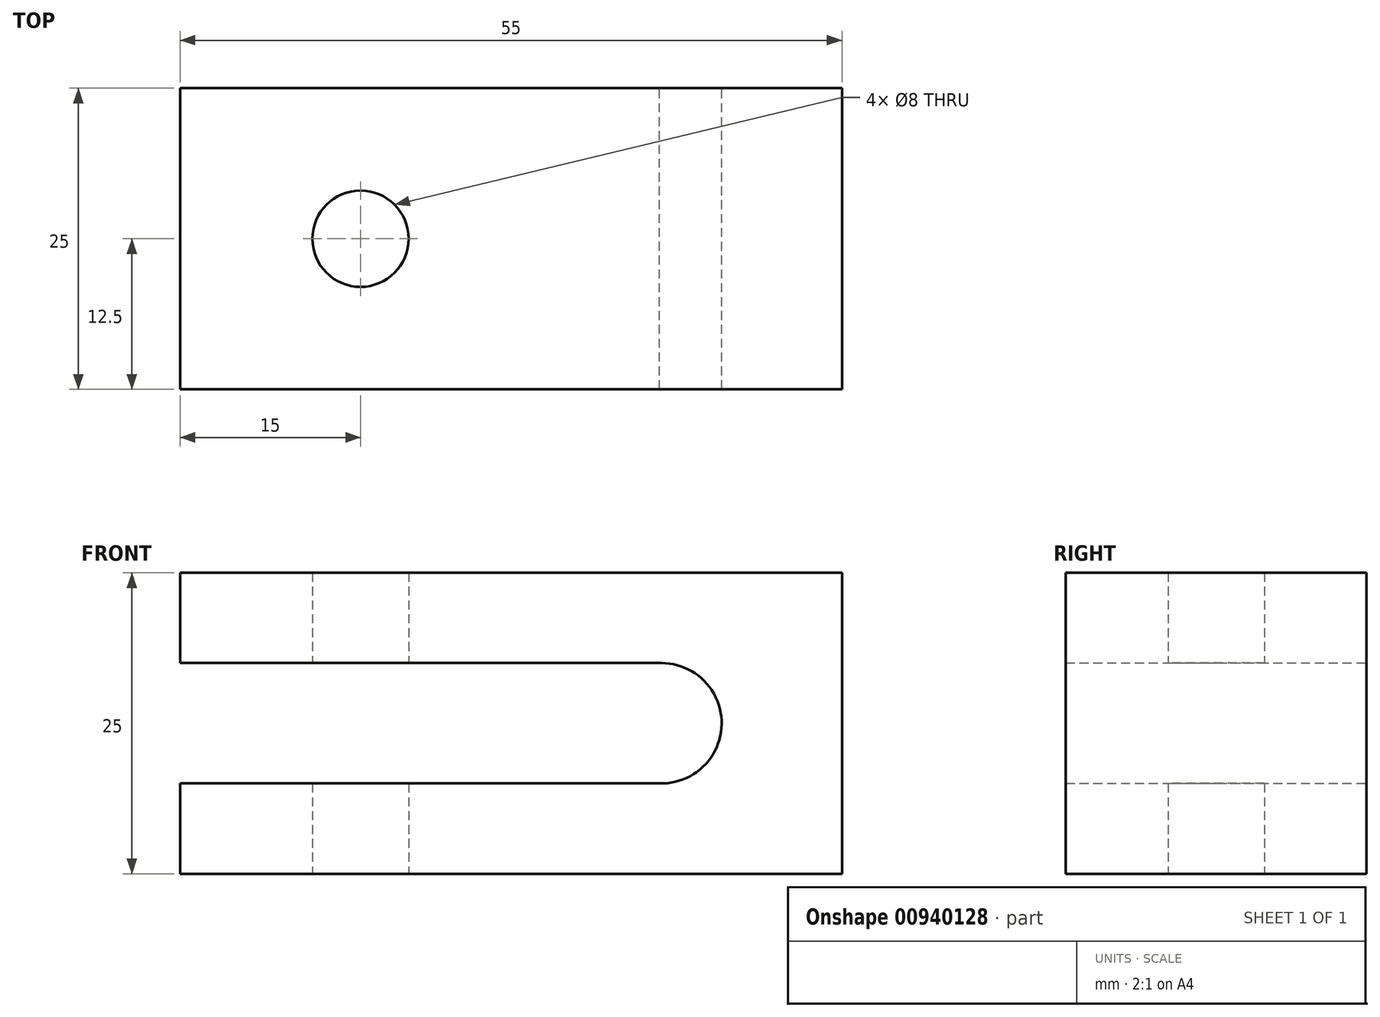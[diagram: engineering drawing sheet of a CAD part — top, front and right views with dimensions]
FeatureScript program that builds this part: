
annotation { "Feature Type Name" : "Feature", "Feature Type Description" : "" }
export const myFeature = defineFeature(function(context is Context, id is Id, definition is map)
    precondition{}
    {
        {
            var Q0;
            Q0=qCreatedBy(makeId("Front.planeOp"),FACE);
            var sketch = newSketch(context, id + "F0", { "sketchPlane" : qUnion([Q0])});
            skLineSegment(sketch, "E0.bottom", {"start": v(-27.5, 12.5) * mm, "end": v(27.5, 12.5) * mm});
            skLineSegment(sketch, "E0.top", {"start": v(-27.5, -12.5) * mm, "end": v(27.5, -12.5) * mm});
            skLineSegment(sketch, "E0.left", {"start": v(-27.5, 12.5) * mm, "end": v(-27.5, 5) * mm});
            skLineSegment(sketch, "E0.right", {"start": v(27.5, 12.5) * mm, "end": v(27.5, -12.5) * mm});
            skPoint(sketch, "E0.middle", {"position": v(0, 0) * mm});
            skArc(sketch, "E1", {"start": v(12.32, -5) * mm, "mid": v(17.5, -0.08) * mm, "end": v(12.49, 5) * mm});
            skLineSegment(sketch, "E2", {"start": v(12.68, -5) * mm, "end": v(-27.5, -5) * mm});
            skPoint(sketch, "E3.orphan", {"position": v(-27.5, 0) * mm});
            skLineSegment(sketch, "E4", {"start": v(12.51, 5) * mm, "end": v(-27.5, 5) * mm});
            skLineSegment(sketch, "E5.trimOffspring", {"start": v(-27.5, -5) * mm, "end": v(-27.5, -12.5) * mm});
            skSolve(sketch);
        }
        {
            var Q0;
            Q0=makeQuery(id+"F0.imprint","IMPRINT",FACE,{"disambiguationData":[TD([[makeQuery(id+"F0.imprint","IMPRINT",EDGE,{"derivedFrom":sQuery(id+"F0.wireOp",EDGE,"E0.bottom")}),-1.0]])]});
            extrude(context, id + "F1", {"entities" : qUnion([Q0]), "depth" : 25 * mm, "offsetDistance" : 25 * mm});
        }
        {
            var Q0;
            Q0=makeQuery(id+"F1.opExtrude","SWEPT_FACE",FACE,{"disambiguationData":[OSD([sQuery(id+"F0.wireOp",EDGE,"E0.top")])]});
            var sketch = newSketch(context, id + "F2", { "sketchPlane" : qUnion([Q0])});
            skCircle(sketch, "E6", {"center": v(-12.5, 12.5) * mm, "radius": 4 * mm});
            skPoint(sketch, "E7.orphan", {"position": v(-27.5, 12.5) * mm});
            skSolve(sketch);
        }
        {
            var Q0;
            Q0=makeQuery(id+"F2.imprint","IMPRINT",FACE,{"disambiguationData":[TD([[makeQuery(id+"F2.imprint","IMPRINT",EDGE,{"derivedFrom":sQuery(id+"F2.wireOp",EDGE,"E6")}),1.0]])]});
            extrude(context, id + "F3", {"entities" : qUnion([Q0]), "operationType" : NewBodyOperationType.REMOVE, "oppositeDirection" : true, "depth" : 25 * mm, "offsetDistance" : 25 * mm});
        }
    });
